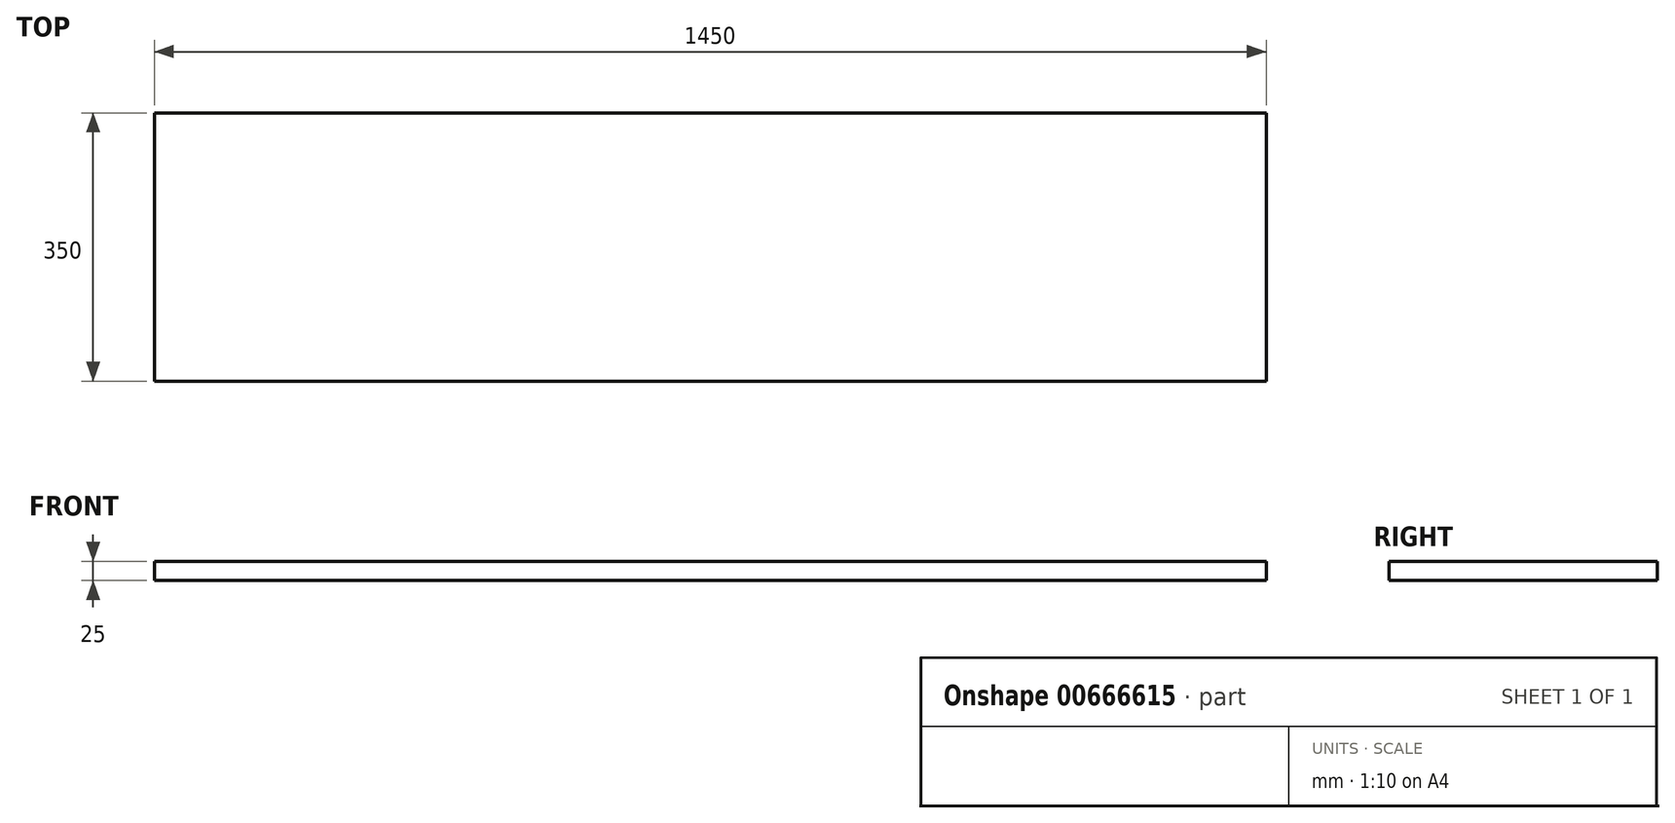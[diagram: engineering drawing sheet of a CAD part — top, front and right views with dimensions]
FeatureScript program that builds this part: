
annotation { "Feature Type Name" : "Feature", "Feature Type Description" : "" }
export const myFeature = defineFeature(function(context is Context, id is Id, definition is map)
    precondition{}
    {
        {
            var Q0;
            Q0=qCreatedBy(makeId("Top.planeOp"),FACE);
            var sketch = newSketch(context, id + "F0", { "sketchPlane" : qUnion([Q0])});
            skLineSegment(sketch, "E0.bottom", {"start": v(0, 0) * mm, "end": v(-1450, 0) * mm});
            skLineSegment(sketch, "E0.top", {"start": v(0, 350) * mm, "end": v(-1450, 350) * mm});
            skLineSegment(sketch, "E0.left", {"start": v(0, 0) * mm, "end": v(0, 350) * mm});
            skLineSegment(sketch, "E0.right", {"start": v(-1450, 0) * mm, "end": v(-1450, 350) * mm});
            skSolve(sketch);
        }
        {
            var Q0;
            Q0 = qSketchRegion(id + "F0", true);
            extrude(context, id + "F1", {"entities" : qUnion([Q0]), "depth" : 25 * mm, "offsetDistance" : 25 * mm});
        }
    });
